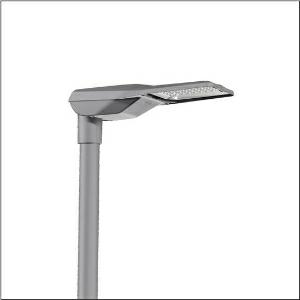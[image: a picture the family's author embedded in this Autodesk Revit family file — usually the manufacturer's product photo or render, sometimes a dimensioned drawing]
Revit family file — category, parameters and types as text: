
# Revit family: streetlight_sl_21_iq_mini___p0_5a_5xe2v31d08jb_3bf9
name_source: partatom
category: Lighting Fixtures
units: mm (PartAtom-declared; Revit-internal decimal feet)

## family parameters
Cut with Voids When Loaded = No
Host = Face
Light Source = No
Part Type = Normal
Room Calculation Point = No
Round Connector Dimension = Use Diameter
Shared = No

## types (1)
- --- (1 x LED, 10640 lm, 71.6 W, 3000K)
    Apparent Load = 72 VA
    CIE Flux Codes = 37 73 96 100 100
    Color Rendering = 70
    Color Temperature = 3000K
    Default Elevation = 1800 mm
    Description = Streetlight SL 21 iQ mini, mast luminaire, primary light control with lens, of PMMA, primary optical cover: cover, of toughened safety glass, transparent, light distribution: P0.5a, light emission: direct distribution, primary light characteristic: asymmetric, installation type: post-top, side-entry, LED, High Power LED, rated luminous flux: 10.640lm, luminous efficacy: 149lm/W, light colour: 730, colour temperature: 3000K, control gear: iQ-Comfort, control: pre-setting: linear dimming characteristic, Auto-Match, Temp-Guard, Lumen-Switch, Night-Set, Smart-Wire, Light-Fading, Desk-Remote (wireless, voltage-free reading and setting of iQ features in the workshop via application-optimized NFC function/RFID function), optimised constant luminous flux control (CLO 2.0), mains connection: 220..240V, AC, 50/60Hz, start of lifetime: 72W, end of service life: 75W, reduction: 33W, luminaire housing, of diecast aluminium, powder-coated, Siteco® metallic grey (DB 702S), corrosivity category C5 mid according to DIN EN ISO 12944, please order mast flange separately, inclination adjustable: 0°, 5°, 10°, 15°, sealing non-destructively replaceable, multi-level sealing system, length: 628mm, width: 235mm, height: 110mm, mast flange for spigot size: 42mm (side-entry): 5XC10008XM4, 60/48mm (side-entry/post-top): 5XC10108XM2, 76/60mm (side-entry/post-top): 5XC10108XM1, mounting height: 4..8m, protection rating (complete): IP66, insulation class (complete): insulation class II (safety insulation), certification: CE, ENEC, ENEC+, VDE, impact resistance: IK10, permissible operating ambient temperature for outdoor applications: -40..+50°C, standard-compliant lighting for roads and squares, packaging unit: 1 piece

Light Distribution: P0.5a
    Height = 110 mm
    Lamp = 1 x LED
    Lamp Light Flux = 10640 lm
    Lamp Power = 71.6 W
    Lamp count = 1
    Length = 625 mm
    Luminous efficacy = 149 lm/W
    Manufacturer = Siteco
    ModVariant = No
    Model = 5XE2V31D08JB
    Number of Poles = 1
    OnlyDefault = Yes
    Power Factor = 1
    Product Name = Streetlight SL 21 iQ mini | P0.5a
    Product group = mast luminaire | pylon top
    ProductGroupID = 6100
    Protection Class = Protection class II
    Protection Degree = IP 66
    RLX_Detail_Level = 1
    RLX_Emergency_Light_Flux = 0 lm
    RLX_Emergency_Type = 0
    RLX_Emergency_Type_DB = No
    RlxData = <blob elided: 92101 chars, md5=97fa623e>
    Socket = socket
    Standby Power = 0 W
    System Light Flux = 10640 lm
    System Power = 72 W
    Type Comments = factory setting: luminous flux: 100 % | dim-lin: 254 | 746 mA
    Type Image = l_1003519.jpg
    URL = http://relux.com
    VarID = @adj_090759
    Voltage = 0 V
    Weight = 0.00 kg
    Width = 234 mm

## geometry (parser evidence)
native form markers: Blend x4, Sweep x10
no freeform markers — native parametric forms only
